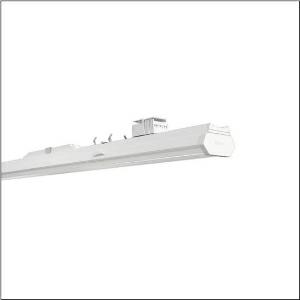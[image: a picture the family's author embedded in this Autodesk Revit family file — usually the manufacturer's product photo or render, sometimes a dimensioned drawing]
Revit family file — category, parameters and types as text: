
# Revit family: licross_r__11_protected_mo_51ts12dn48xfd_9faa
name_source: partatom
category: Lighting Fixtures
units: mm (PartAtom-declared; Revit-internal decimal feet)

## family parameters
Cut with Voids When Loaded = No
Host = Face
Light Source = No
Part Type = Normal
Room Calculation Point = No
Round Connector Dimension = Use Diameter
Shared = No

## types (1)
- --- (1 x LED, 1320 lm, 10 W, 4000K)
    Apparent Load = 10 VA
    CIE Flux Codes = 54 82 95 97 100
    Color Rendering = 80
    Color Temperature = 4000K
    Default Elevation = 1800 mm
    Description = Licross® 11 Protected MOluminaire insert, length: 1.500mm, width: 90mm, height: 101mm, LED rated luminous flux: 8.470lm, light colour: 840, control gear: DALI 2, control gear: ECG DALI, with plug, 6-pole, with phase selection, mains connection: 220..240V, AC/DC, 0/50..60Hz, without changeover relay, for emergency light function, for central battery installations according to DIN EN 60598-2-22, halogen-free wiring, primary optical cover: cover, of PMMA, light emission: direct with ceiling illumination distribution, protection rating (complete): IP50, insulation class (complete): insulation class I (protective earthing), certification: CE, ENEC, VDE, protection symbol: D if used in an environment without relevant dust loads with corresponding accessories, permissible ambient temperature for indoor applications: -25..+40°C, standard: EN 60598-2-22, reducing of maximum allowable ambient temperature of 5°C with ceiling mounting, corresponds to IFS (International Featured Standards) requirements for safety and quality in the food industry, packaging unit: 1 piece
    Height = 92 mm
    Lamp = 1 x LED
    Lamp Light Flux = 1320 lm
    Lamp Power = 10 W
    Lamp count = 1
    Length = 1500 mm
    Luminous efficacy = 132 lm/W
    Manufacturer = Siteco
    ModVariant = No
    Model = 51TS12DN48XFD
    Mounting Place = Ceiling
    Mounting Type = Pendant
    Number of Poles = 1
    OnlyDefault = Yes
    Power Factor = 1
    Product Name = Licross® 11 Protected MO
    Product group = luminaire insert
    ProductGroupID = 902
    Protection Class = Protection class I
    Protection Degree = IP 50
    RLX_Detail_Level = 1
    RlxData = <blob elided: 24313 chars, md5=f3a15238>
    Socket = socket
    Standby Power = 0 W
    System Light Flux = 1320 lm
    System Power = 10 W
    Type Comments = : DC mode (central or group accumulator) initial emergency light level
    Type Image = l_1256145.jpg
    URL = http://relux.com
    VarID = @adj_134845
    Voltage = 0 V
    Weight = 0.00 kg
    Width = 88 mm

## geometry (parser evidence)
native form markers: Blend x4, Sweep x9
no freeform markers — native parametric forms only
